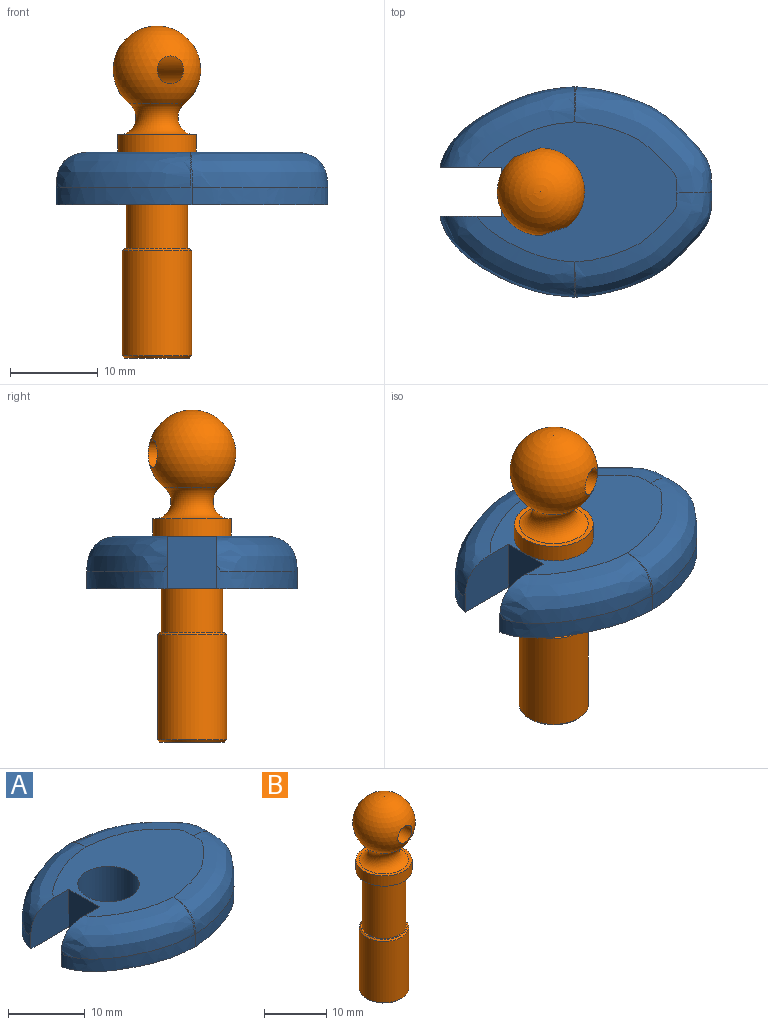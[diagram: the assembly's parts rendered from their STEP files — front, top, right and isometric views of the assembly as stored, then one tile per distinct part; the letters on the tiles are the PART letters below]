
ASSEMBLY  parts=2 mates=1
PART A: 16 faces, bbox 31.7x24.4x6.4 mm
  f0: plane 7x6mm, normal (0,-1,0), area 39.3mm2, adj f1,f6,f7,f8,f14
  f1: plane 6x5.6mm, normal (-1,0,0), area 33.6mm2, adj f0,f2,f7,f8
  f2: plane 7x6mm, normal (0,1,0), area 39.3mm2, adj f1,f3,f7,f8,f9
  f3: extruded ~15.5x9.2mm, area 38.5mm2, adj f2,f4,f8,f9,f10
  f4: extruded ~15.5x12mm, area 43.1mm2, adj f3,f5,f8,f11
  f5: extruded ~15.5x12mm, area 43.1mm2, adj f4,f6,f8,f12
  f6: extruded ~15.5x9.2mm, area 38.5mm2, adj f0,f5,f8,f13,f14
  f7: plane 23.17x16.37mm, normal (0,0,1), area 216mm2, adj f0,f1,f2,f9,f11,f12,f14,f15
  f8: plane 31.08x24.04mm, normal (0,0,-1), area 491.9mm2, adj f0,f1,f2,f3,f4,f5,f6,f15
  f9: bspline ~15.87x10.03mm, area 108.8mm2, adj f2,f3,f7,f10
  f10: bspline ~4.01x4mm, area 0.9mm2, adj f3,f9,f11
  f11: bspline ~15.78x12.17mm, area 125.1mm2, adj f4,f7,f10,f12
  f12: bspline ~15.78x12.13mm, area 125mm2, adj f5,f7,f11,f13
  f13: bspline ~4.01x4mm, area 0.6mm2, adj f6,f12,f14
  f14: bspline ~15.87x10.03mm, area 108.9mm2, adj f0,f6,f7,f13
  f15: cylinder r=4mm len=8mm, axis (0,0,1), area 150.8mm2, adj f7,f8
PART B: 12 faces, bbox 10x10x37.9 mm
  f0: cylinder r=4.5mm len=9mm, axis (0,0,-1), area 56.5mm2, adj f1,f2
  f1: plane 9x9mm, normal (0,0,1), area 15mm2, adj f0,f10
  f2: plane 9x9mm, normal (0,0,-1), area 25.1mm2, adj f0,f3
  f3: cylinder r=3.5mm len=11mm, axis (0,0,1), area 241.9mm2, adj f2,f6
  f4: cylinder r=3.95mm len=12mm, axis (0,0,1), area 297.8mm2, adj f7,f8
  f5: plane 7.4x7.4mm, normal (0,0,-1), area 43mm2, adj f8
  f6: plane 7.4x7.4mm, normal (0,0,1), area 4.5mm2, adj f3,f7
  f7: cone r=3.95mm half-angle=45deg, axis (0,0,-1), area 8.5mm2, adj f4,f6
  f8: cone r=3.7mm half-angle=45deg, axis (0,0,1), area 8.5mm2, adj f4,f5
  f9: sphere r=5mm, area 263mm2, adj f10,f11
  f10: torus R=4.4mm, axis (0,0,-1), area 79.1mm2, adj f1,f9
  f11: cylinder r=1.59mm len=9.48mm, axis (0,-1,0), area 94.6mm2, adj f9
PLACE A t=(-15.47,-2.85,-4.99)mm fixed
PLACE B rot(axis=(0,0,1),18.9deg) t=(-14.85,-6.57,-4.99)mm
MATE revolute A.f15 <-> B.f0  axis (0,0,1) through (-3.97,-2.85,1.01)mm
